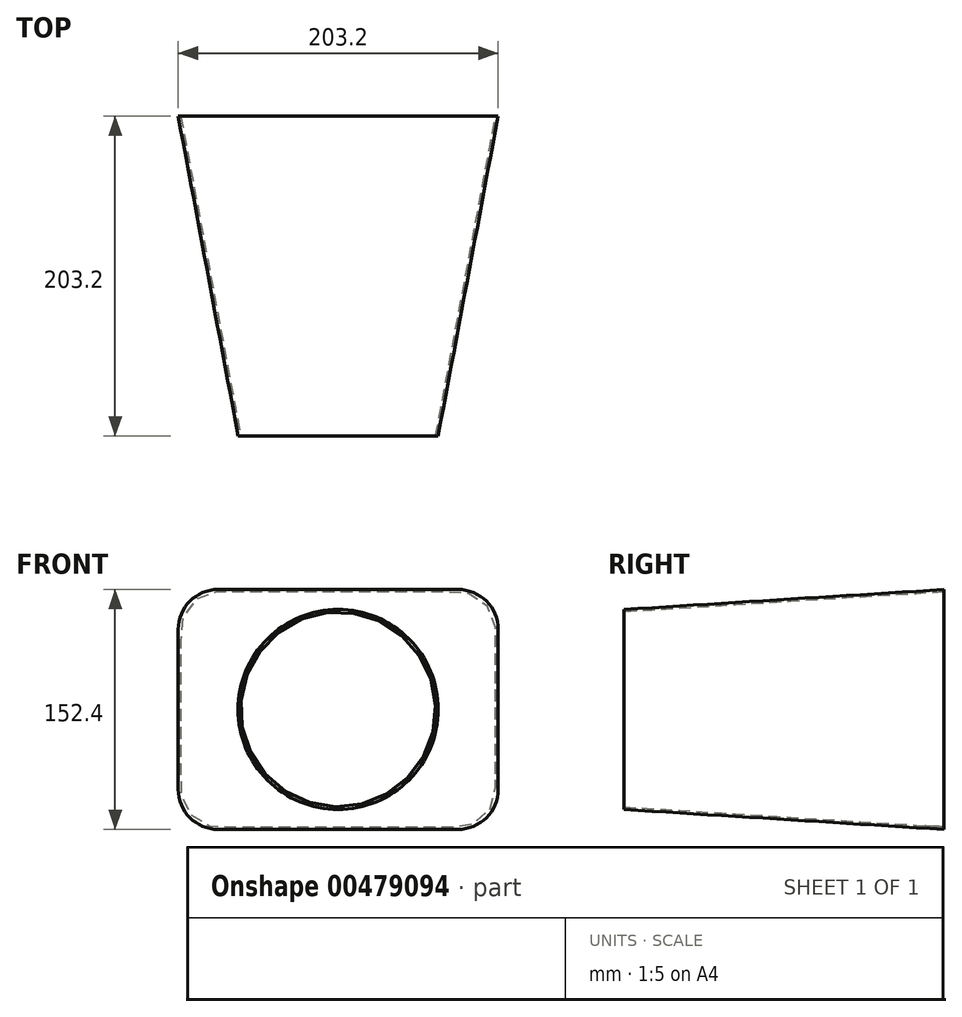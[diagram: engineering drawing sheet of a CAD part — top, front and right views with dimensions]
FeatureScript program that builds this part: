
annotation { "Feature Type Name" : "Feature", "Feature Type Description" : "" }
export const myFeature = defineFeature(function(context is Context, id is Id, definition is map)
    precondition{}
    {
        {
            var Q0;
            Q0=qCreatedBy(makeId("Front.planeOp"),FACE);
            var sketch = newSketch(context, id + "F0", { "sketchPlane" : qUnion([Q0])});
            skLineSegment(sketch, "E0.bottom", {"start": v(-76.2, -76.2) * mm, "end": v(76.2, -76.2) * mm});
            skLineSegment(sketch, "E0.top", {"start": v(-76.2, 76.2) * mm, "end": v(76.2, 76.2) * mm});
            skLineSegment(sketch, "E0.left", {"start": v(-101.6, -50.8) * mm, "end": v(-101.6, 50.8) * mm});
            skLineSegment(sketch, "E0.right", {"start": v(101.6, -50.8) * mm, "end": v(101.6, 50.8) * mm});
            skPoint(sketch, "E0.middle", {"position": v(0, 0) * mm});
            skPoint(sketch, "E1.visualSharp", {"position": v(-101.6, -76.2) * mm});
            skArc(sketch, "E1.filletArc", {"start": v(-101.6, -50.8) * mm, "mid": v(-94.16, -68.76) * mm, "end": v(-76.2, -76.2) * mm});
            skPoint(sketch, "E2.visualSharp", {"position": v(-101.6, 76.2) * mm});
            skArc(sketch, "E2.filletArc", {"start": v(-76.2, 76.2) * mm, "mid": v(-94.16, 68.76) * mm, "end": v(-101.6, 50.8) * mm});
            skPoint(sketch, "E3.visualSharp", {"position": v(101.6, -76.2) * mm});
            skArc(sketch, "E3.filletArc", {"start": v(76.2, -76.2) * mm, "mid": v(94.16, -68.76) * mm, "end": v(101.6, -50.8) * mm});
            skPoint(sketch, "E4.visualSharp", {"position": v(101.6, 76.2) * mm});
            skArc(sketch, "E4.filletArc", {"start": v(101.6, 50.8) * mm, "mid": v(94.16, 68.76) * mm, "end": v(76.2, 76.2) * mm});
            skSolve(sketch);
        }
        {
            var Q0;
            Q0=qCreatedBy(makeId("Front.planeOp"),FACE);
            var sketch = newSketch(context, id + "F1", { "sketchPlane" : qUnion([Q0])});
            skSolve(sketch);
        }
        {
            var Q0;
            Q0=qCreatedBy(makeId("Front.planeOp"),FACE);
            var Q1;
            Q1 = qBodyType(qCreatedBy(id + "F1" ,EDGE), BodyType.WIRE);
            cPlane(context, id + "F2", {"entities" : qUnion([Q0, Q1]), "cplaneType" : CPlaneType.OFFSET, "offset" : 203.2 * mm, "width" : 152.4 * mm, "height" : 152.4 * mm});
        }
        {
            var Q0;
            Q0=qCreatedBy(id+"F2.planeOp",FACE);
            var sketch = newSketch(context, id + "F3", { "sketchPlane" : qUnion([Q0])});
            skCircle(sketch, "E5", {"center": v(0, 0) * mm, "radius": 63.5 * mm});
            skSolve(sketch);
        }
        {
            var Q0;
            Q0=makeQuery(id+"F0.imprint","IMPRINT",FACE,{"disambiguationData":[TD([[makeQuery(id+"F0.imprint","IMPRINT",EDGE,{"derivedFrom":sQuery(id+"F0.wireOp",EDGE,"E0.bottom")}),1.0]])]});
            var Q1;
            Q1=makeQuery(id+"F3.imprint","IMPRINT",FACE,{"disambiguationData":[TD([[makeQuery(id+"F3.imprint","IMPRINT",EDGE,{"derivedFrom":sQuery(id+"F3.wireOp",EDGE,"E5")}),1.0]])]});
            loft(context, id + "F4", {"sheetProfilesArray" : [{ "sheetProfileEntities" : qUnion([Q0]) }, { "sheetProfileEntities" : qUnion([Q1]) }]});
        }
        {
            var Q0;
            Q0=makeQuery(id+"F4.opLoft","CAP_FACE",FACE,{"disambiguationData":[OSD([makeQuery(id+"F3.imprint","IMPRINT",FACE,{"disambiguationData":[TD([[makeQuery(id+"F3.imprint","IMPRINT",EDGE,{"derivedFrom":sQuery(id+"F3.wireOp",EDGE,"E5")}),1.0]])]})])],"isStart":true});
            var Q1;
            Q1=makeQuery(id+"F4.opLoft","CAP_FACE",FACE,{"disambiguationData":[OSD([makeQuery(id+"F0.imprint","IMPRINT",FACE,{"disambiguationData":[TD([[makeQuery(id+"F0.imprint","IMPRINT",EDGE,{"derivedFrom":sQuery(id+"F0.wireOp",EDGE,"E0.bottom")}),1.0]])]})])],"isStart":true});
            shell(context, id + "F5", {"entities" : qUnion([Q0, Q1]), "thickness" : 1.59 * mm});
        }
    });
